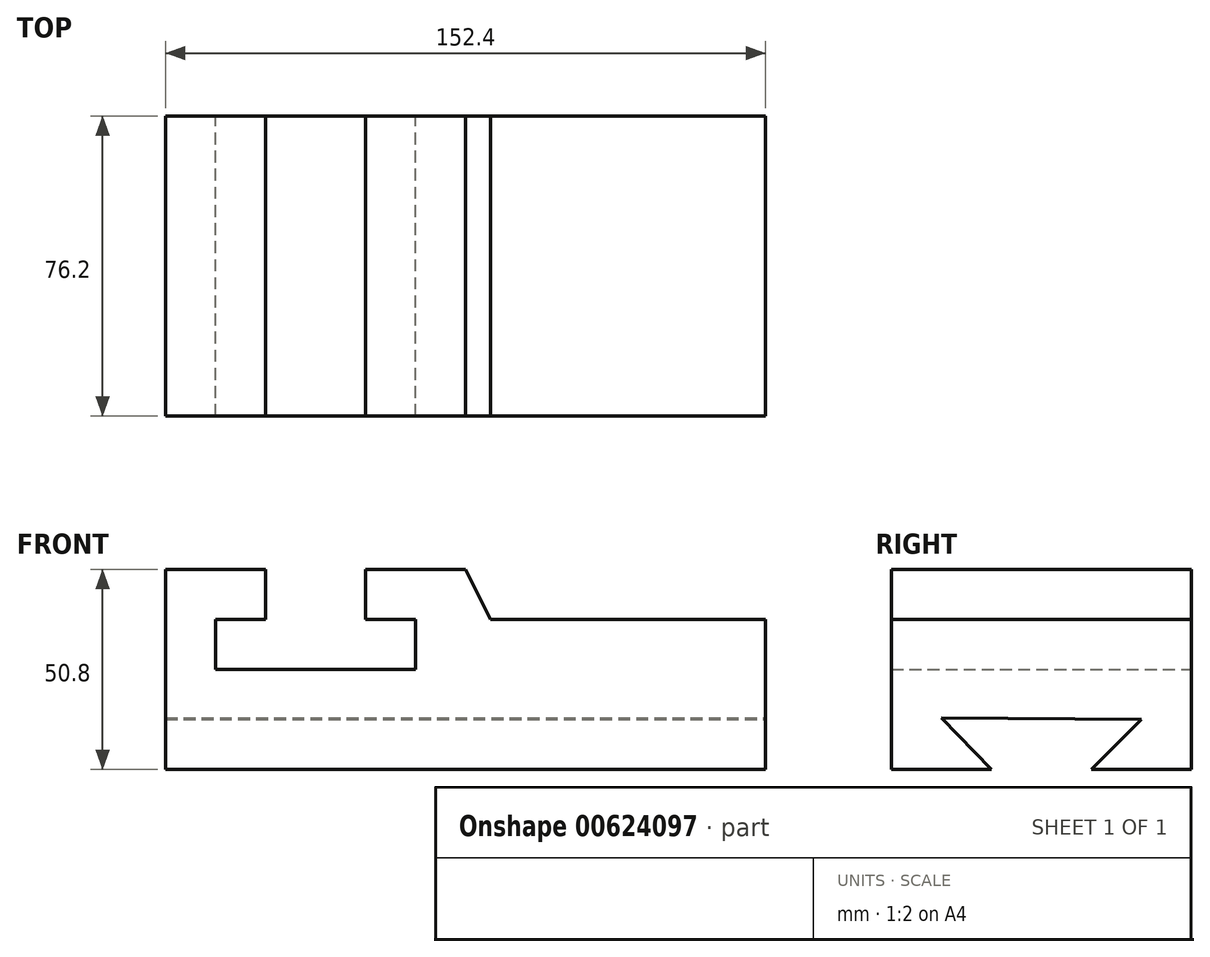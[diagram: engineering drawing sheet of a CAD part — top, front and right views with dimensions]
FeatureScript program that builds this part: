
annotation { "Feature Type Name" : "Feature", "Feature Type Description" : "" }
export const myFeature = defineFeature(function(context is Context, id is Id, definition is map)
    precondition{}
    {
        {
            var Q0;
            Q0=qCreatedBy(makeId("Front.planeOp"),FACE);
            var sketch = newSketch(context, id + "F0", { "sketchPlane" : qUnion([Q0])});
            skLineSegment(sketch, "E0.bottom", {"start": v(0, 0) * mm, "end": v(152.4, 0) * mm});
            skLineSegment(sketch, "E0.left", {"start": v(0, 0) * mm, "end": v(0, 50.8) * mm});
            skLineSegment(sketch, "E1", {"start": v(0, 50.8) * mm, "end": v(25.4, 50.8) * mm});
            skLineSegment(sketch, "E2", {"start": v(25.4, 50.8) * mm, "end": v(25.4, 38.1) * mm});
            skLineSegment(sketch, "E3", {"start": v(25.4, 38.1) * mm, "end": v(12.7, 38.1) * mm});
            skLineSegment(sketch, "E4", {"start": v(12.7, 38.1) * mm, "end": v(12.7, 25.4) * mm});
            skLineSegment(sketch, "E5", {"start": v(12.7, 25.4) * mm, "end": v(63.5, 25.4) * mm});
            skLineSegment(sketch, "E6", {"start": v(63.5, 25.4) * mm, "end": v(63.5, 38.1) * mm});
            skLineSegment(sketch, "E7", {"start": v(63.5, 38.1) * mm, "end": v(50.8, 38.1) * mm});
            skLineSegment(sketch, "E8", {"start": v(50.8, 38.1) * mm, "end": v(50.8, 50.8) * mm});
            skLineSegment(sketch, "E9", {"start": v(50.8, 50.8) * mm, "end": v(76.2, 50.8) * mm});
            skLineSegment(sketch, "E10", {"start": v(76.2, 50.8) * mm, "end": v(82.55, 38.1) * mm});
            skLineSegment(sketch, "E11", {"start": v(82.55, 38.1) * mm, "end": v(152.4, 38.1) * mm});
            skLineSegment(sketch, "E12", {"start": v(152.4, 38.1) * mm, "end": v(152.4, 0) * mm});
            skSolve(sketch);
        }
        {
            var Q0;
            Q0 = qSketchRegion(id + "F0", true);
            extrude(context, id + "F1", {"entities" : qUnion([Q0]), "depth" : 76.2 * mm, "offsetDistance" : 25.4 * mm});
        }
        {
            var Q0;
            Q0=makeQuery(id+"F1.opExtrude","SWEPT_FACE",FACE,{"disambiguationData":[OSD([sQuery(id+"F0.wireOp",EDGE,"E12")])]});
            var sketch = newSketch(context, id + "F2", { "sketchPlane" : qUnion([Q0])});
            skLineSegment(sketch, "E13", {"start": v(-76.2, 0) * mm, "end": v(-76.2, 13.1) * mm});
            skLineSegment(sketch, "E14", {"start": v(-63.5, 13.1) * mm, "end": v(-50.8, 0) * mm});
            skLineSegment(sketch, "E15", {"start": v(-50.8, 0) * mm, "end": v(-76.2, 0) * mm});
            skLineSegment(sketch, "E16", {"start": v(0, 0) * mm, "end": v(-25.4, 0) * mm});
            skLineSegment(sketch, "E17", {"start": v(-25.4, 0) * mm, "end": v(-12.7, 12.7) * mm});
            skLineSegment(sketch, "E18", {"start": v(0, 12.7) * mm, "end": v(0, 0) * mm});
            skLineSegment(sketch, "E19", {"start": v(-63.5, 13.1) * mm, "end": v(-12.7, 12.7) * mm});
            skLineSegment(sketch, "E20", {"start": v(-50.8, 0) * mm, "end": v(-25.4, 0) * mm});
            skSolve(sketch);
        }
        {
            var Q0;
            Q0 = qSketchRegion(id + "F2", true);
            extrude(context, id + "F3", {"entities" : qUnion([Q0]), "operationType" : NewBodyOperationType.REMOVE, "oppositeDirection" : true, "depth" : 152.4 * mm, "offsetDistance" : 25.4 * mm});
        }
    });
